# Revit family: Fixture_Control-Lutron-Quantum-QP2
name_source: partatom
category: Electrical Equipment
revit_build: Autodesk Revit 2017 (Build: 20160720_1515(x64)
units: mm (PartAtom-declared; Revit-internal decimal feet)

## family parameters
Cut with Voids When Loaded = No
Host = Face
OmniClass Number = 23.85.80.11
OmniClass Title = Building Controls
Part Type = Other Panel
Room Calculation Point = No
Round Connector Dimension = Use Diameter
Shared = No

## types (1)
- 120V
    Apparent Power = 120 VA
    Assembly Code = D5020200
    Cost = 0 $
    Current = 1 A
    Default Elevation = 4' - 0"
    Description = Light Management Hub
    Electrical Potential = 120 V
    Frequency = 60 Hz
    Instruction Sheet Link = http://www.lutron.com
    Load Classification = Power
    Manufacturer = Lutron Electronics Co., Inc
    Manufacturer Fax Number = 610-282-1243
    Material = Steel - Lutron - Black
    Model = QP2-120
    Number of Poles = 1
    Overall Depth = 0' - 5 31/32"
    Overall Height = 2' - 7 1/2"
    Overall Width = 1' - 3 3/4"
    Performance URL = http://www.lutron.com
    Phase = 1
    Product Documentation Link = http://www.lutron.com
    Product Name = Centralized Control Equipment - QP2
    Product Page URL = http://www.lutron.com
    Series = Quantum
    URL = http://www.lutron.com
    Unit Weight = 40.00 lb
    Version = 2017 - v1.0b
    Video Link = https://www.youtube.com
    Voltage = 120.00 V
    Warranty URL = http://www.lutron.com

## geometry (parser evidence)
native form markers: Blend x4, Sweep x2
no freeform markers — native parametric forms only
